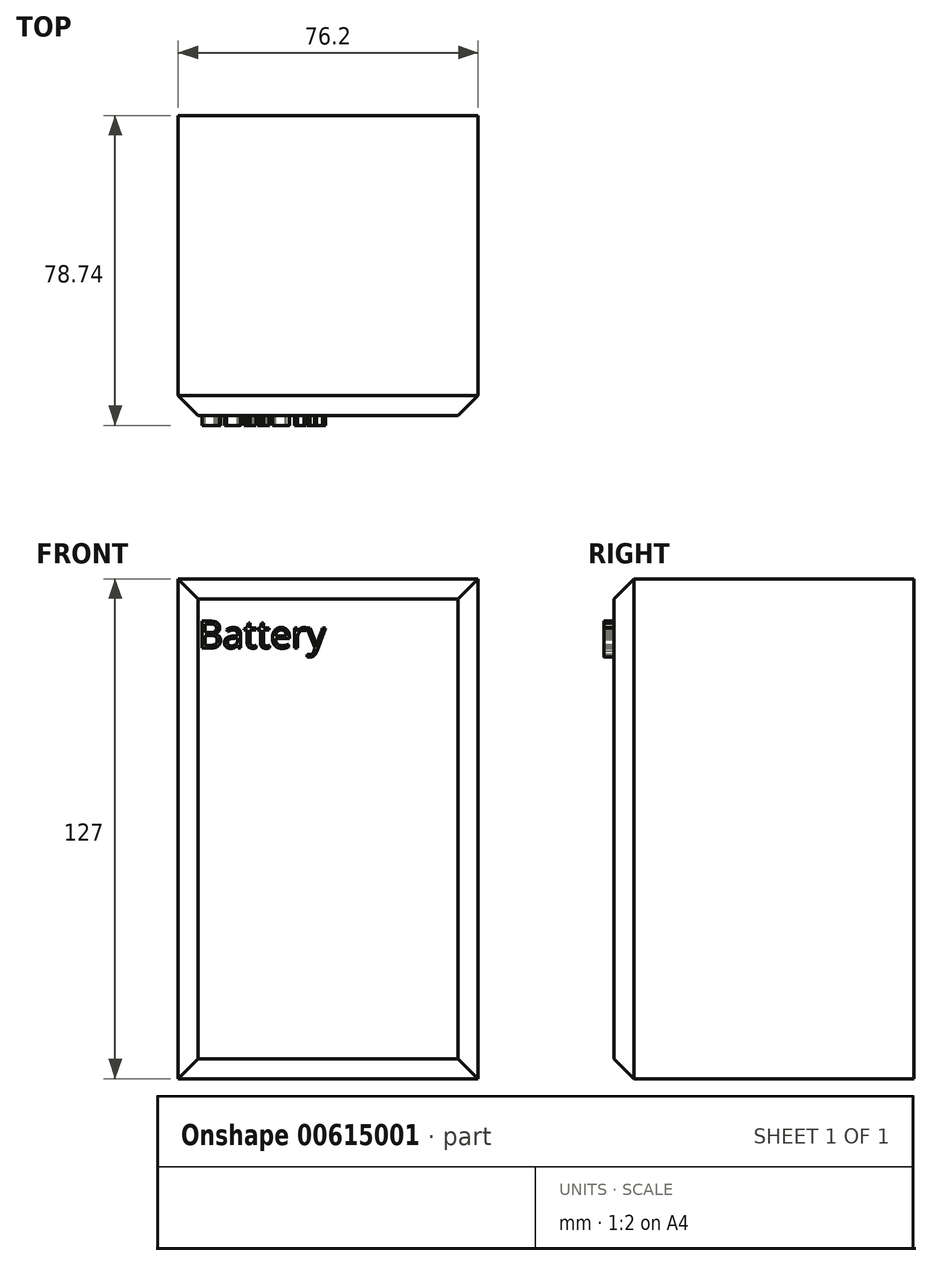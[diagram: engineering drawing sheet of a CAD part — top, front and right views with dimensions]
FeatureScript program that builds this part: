
annotation { "Feature Type Name" : "Feature", "Feature Type Description" : "" }
export const myFeature = defineFeature(function(context is Context, id is Id, definition is map)
    precondition{}
    {
        {
            var Q0;
            Q0=qCreatedBy(makeId("Front.planeOp"),FACE);
            var sketch = newSketch(context, id + "F0", { "sketchPlane" : qUnion([Q0])});
            skLineSegment(sketch, "E0.bottom", {"start": v(-38.1, 63.5) * mm, "end": v(38.1, 63.5) * mm});
            skLineSegment(sketch, "E0.top", {"start": v(-38.1, -63.5) * mm, "end": v(38.1, -63.5) * mm});
            skLineSegment(sketch, "E0.left", {"start": v(-38.1, 63.5) * mm, "end": v(-38.1, -63.5) * mm});
            skLineSegment(sketch, "E0.right", {"start": v(38.1, 63.5) * mm, "end": v(38.1, -63.5) * mm});
            skPoint(sketch, "E0.middle", {"position": v(0, 0) * mm});
            skSolve(sketch);
        }
        {
            var Q0;
            Q0=makeQuery(id+"F0.imprint","IMPRINT",FACE,{"disambiguationData":[TD([[makeQuery(id+"F0.imprint","IMPRINT",EDGE,{"derivedFrom":sQuery(id+"F0.wireOp",EDGE,"E0.bottom")}),-1.0]])]});
            extrude(context, id + "F1", {"entities" : qUnion([Q0]), "depth" : 76.2 * mm, "offsetDistance" : 25.4 * mm});
        }
        {
            var Q0;
            Q0=makeQuery(id+"F1.opExtrude","CAP_EDGE",EDGE,{"disambiguationData":[OSD([sQuery(id+"F0.wireOp",EDGE,"E0.right")])],"isStart":false});
            var Q1;
            Q1=makeQuery(id+"F1.opExtrude","CAP_EDGE",EDGE,{"disambiguationData":[OSD([sQuery(id+"F0.wireOp",EDGE,"E0.bottom")])],"isStart":false});
            var Q2;
            Q2=makeQuery(id+"F1.opExtrude","CAP_EDGE",EDGE,{"disambiguationData":[OSD([sQuery(id+"F0.wireOp",EDGE,"E0.left")])],"isStart":false});
            var Q3;
            Q3=makeQuery(id+"F1.opExtrude","CAP_EDGE",EDGE,{"disambiguationData":[OSD([sQuery(id+"F0.wireOp",EDGE,"E0.top")])],"isStart":false});
            chamfer(context, id + "F2", {"entities" : qUnion([Q0, Q1, Q2, Q3]), "width" : 5.08 * mm, "tangentPropagation" : true});
        }
        {
            var Q0;
            Q0=makeQuery(id+"F1.opExtrude","CAP_FACE",FACE,{"disambiguationData":[OSD([sQuery(id+"F0.wireOp",EDGE,"E0.bottom"),sQuery(id+"F0.wireOp",EDGE,"E0.top"),sQuery(id+"F0.wireOp",EDGE,"E0.left"),sQuery(id+"F0.wireOp",EDGE,"E0.right")])],"isStart":false});
            var sketch = newSketch(context, id + "F3", { "sketchPlane" : qUnion([Q0])});
            skText(sketch, "E1", { "text": "Battery", "fontName": "OpenSans-Regular.ttf"});
            const initialGuessF3  = {"E1": [-0.03302, 0.04591, 1, 0, 0.0069]};
            skSetInitialGuess(sketch, initialGuessF3);
            skSolve(sketch);
        }
        {
            var Q0;
            Q0 = qSketchRegion(id + "F3", true);
            extrude(context, id + "F4", {"entities" : qUnion([Q0]), "operationType" : NewBodyOperationType.ADD, "depth" : 2.54 * mm, "offsetDistance" : 25.4 * mm});
        }
    });
